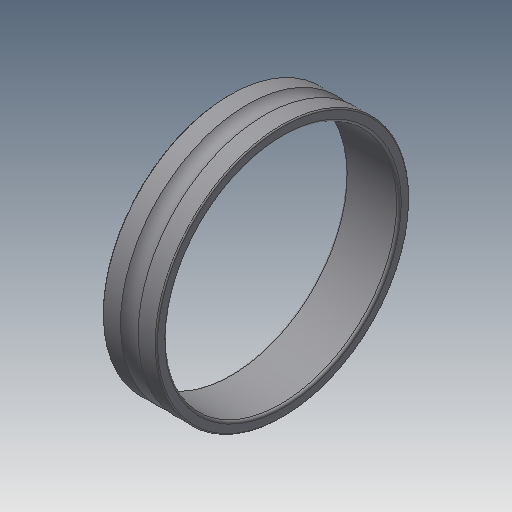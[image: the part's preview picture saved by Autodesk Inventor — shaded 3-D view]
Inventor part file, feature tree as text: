
AUTODESK INVENTOR PART (.ipt)
format: ipt  version: 2019.4 (Build 234330000, 330)  size: 187,904 bytes
history: native  units: mm
features: other x14, revolve x1, sketch x1
ambient origin geometry x8: Origin, YZ Plane, XZ Plane, XY Plane, X Axis, Y Axis, Z Axis, Center Point
bodies: Solid1 (feature_tree)
feature tree (16):
  revolve  "Revolution1"  [1 undecoded]
  other  "1_XY"
  other  "1_YZ"
  other  "1_ZX"
  other  "1_X"
  other  "1_Y"
  other  "1_Z"
  other  "1_Center"
  other  "1_Dummy_XY"
  other  "1_Dummy_YZ"
  other  "1_Dummy_ZX"
  other  "1_Dummy_X"
  other  "1_Dummy_Y"
  other  "1_Dummy_Z"
  other  "1_Dummy_Center"
  sketch  "Sketch_1"  dims[d0=360.0deg d1=0.0mm]
note: 1 required parameter value undecoded (feature->parameter linkage not recoverable at this tier; creation-order binding heuristic only, values carry confidence <= 0.55)
